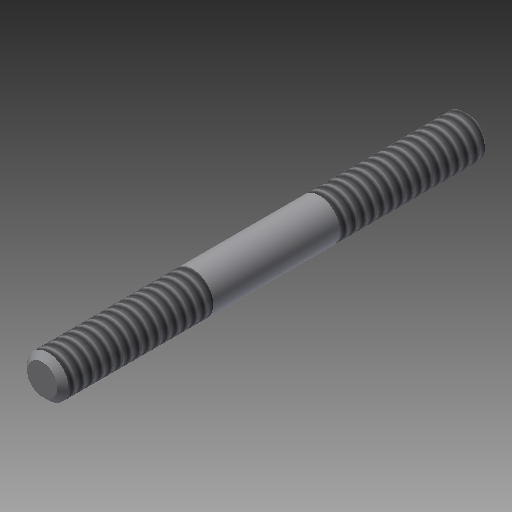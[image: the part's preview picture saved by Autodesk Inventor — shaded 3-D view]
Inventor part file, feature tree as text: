
AUTODESK INVENTOR PART (.ipt)
format: ipt  version: 2019.4 (Build 234330000, 330)  size: 137,216 bytes
history: native  units: in
note: dims shown in document units (in); Inventor stores cm internally (conversion verified against a paired STEP export)
features: other x7, thread x2, revolve x1, sketch x1
ambient origin geometry x8: Origin, YZ Plane, XZ Plane, XY Plane, X Axis, Y Axis, Z Axis, Center Point
bodies: Solid1 (feature_tree)
feature tree (11):
  revolve  "Revolution1"  [1 undecoded]
  thread  "Thread1"  [1 undecoded]
  thread  "Thread2"  [1 undecoded]
  other  "screw_XY"
  other  "screw_YZ"
  other  "screw_ZX"
  other  "screw_X"
  other  "screw_Y"
  other  "screw_Z"
  other  "screw_Center"
  sketch  "Sketch_3"  dims[d0=360.0deg d1=0.4814in d2=0.0in d3=0.4814in d4=0.0in]
note: 3 required parameter values undecoded (feature->parameter linkage not recoverable at this tier; creation-order binding heuristic only, values carry confidence <= 0.55)